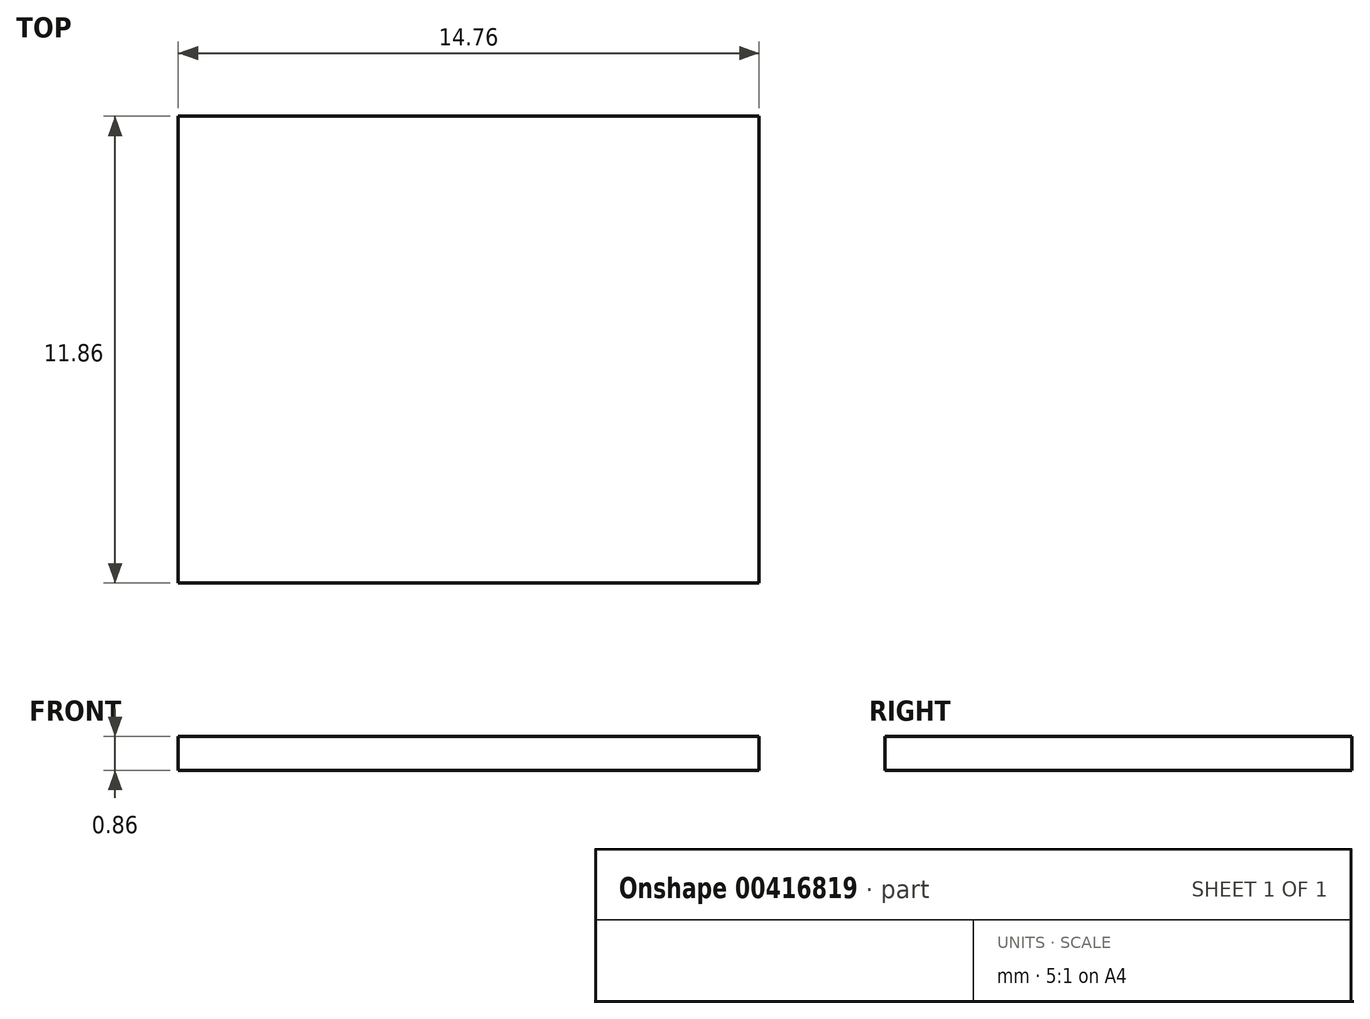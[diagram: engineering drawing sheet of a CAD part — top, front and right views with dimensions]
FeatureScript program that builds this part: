
annotation { "Feature Type Name" : "Feature", "Feature Type Description" : "" }
export const myFeature = defineFeature(function(context is Context, id is Id, definition is map)
    precondition{}
    {
        {
            var Q0;
            Q0=qCreatedBy(makeId("Top.planeOp"),FACE);
            var sketch = newSketch(context, id + "F0", { "sketchPlane" : qUnion([Q0])});
            skLineSegment(sketch, "E0.bottom", {"start": v(0, 0) * mm, "end": v(14.76, 0) * mm});
            skLineSegment(sketch, "E0.top", {"start": v(0, 11.86) * mm, "end": v(14.76, 11.86) * mm});
            skLineSegment(sketch, "E0.left", {"start": v(0, 0) * mm, "end": v(0, 11.86) * mm});
            skLineSegment(sketch, "E0.right", {"start": v(14.76, 0) * mm, "end": v(14.76, 11.86) * mm});
            skSolve(sketch);
        }
        {
            var Q0;
            Q0 = qSketchRegion(id + "F0", true);
            extrude(context, id + "F1", {"entities" : qUnion([Q0]), "depth" : .86 * mm, "offsetDistance" : 25.4 * mm});
        }
    });
